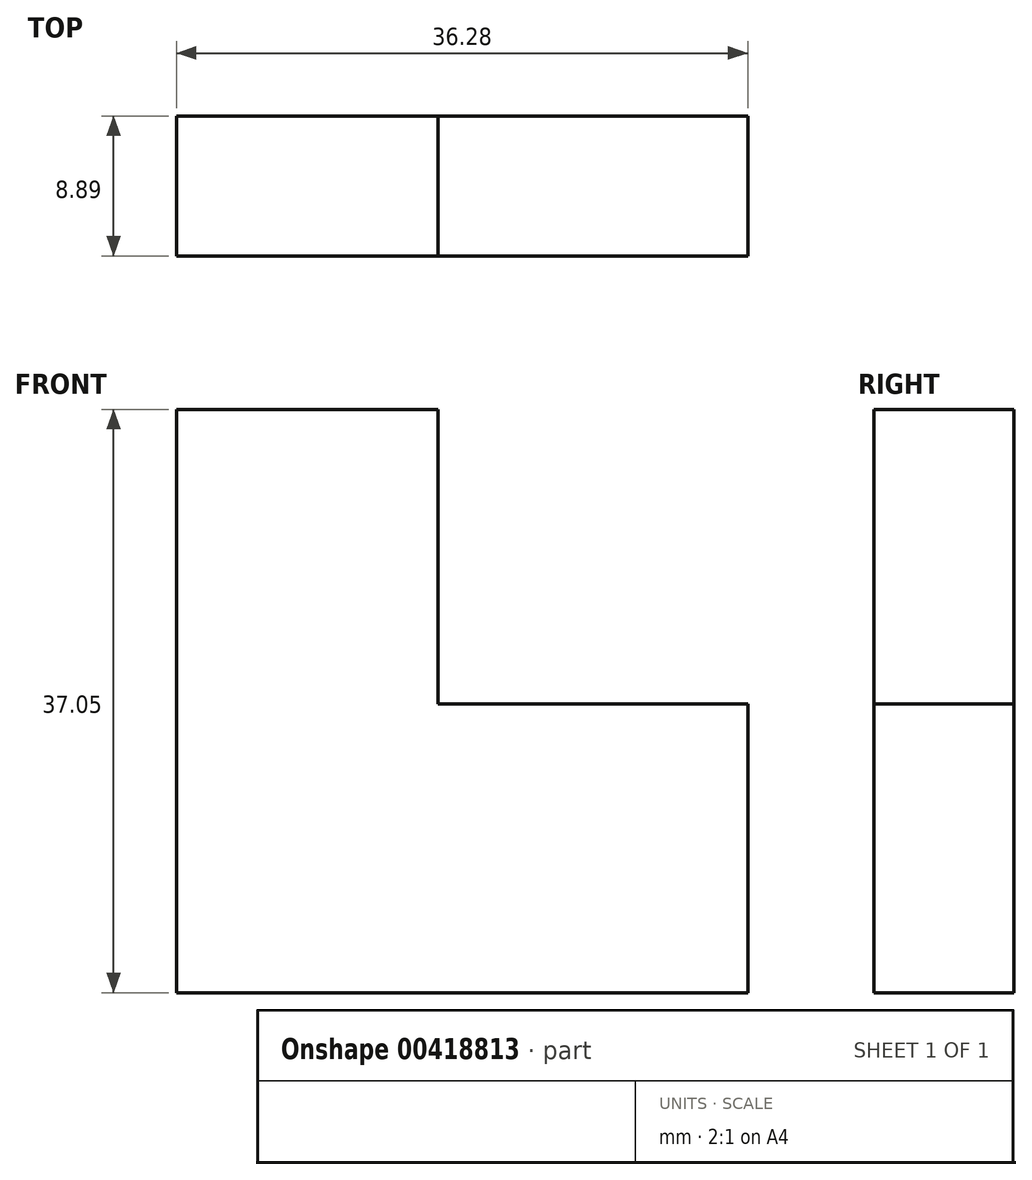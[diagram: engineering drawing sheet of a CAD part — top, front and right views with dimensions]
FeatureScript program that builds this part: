
annotation { "Feature Type Name" : "Feature", "Feature Type Description" : "" }
export const myFeature = defineFeature(function(context is Context, id is Id, definition is map)
    precondition{}
    {
        {
            var Q0;
            Q0=qCreatedBy(makeId("Front.planeOp"),FACE);
            var sketch = newSketch(context, id + "F0", { "sketchPlane" : qUnion([Q0])});
            skLineSegment(sketch, "E0", {"start": v(-36.28, 0) * mm, "end": v(-36.28, 37.05) * mm});
            skLineSegment(sketch, "E1", {"start": v(-36.28, 37.05) * mm, "end": v(-19.67, 37.05) * mm});
            skLineSegment(sketch, "E2", {"start": v(-19.67, 37.05) * mm, "end": v(-19.67, 18.33) * mm});
            skLineSegment(sketch, "E3", {"start": v(-19.67, 18.33) * mm, "end": v(0, 18.33) * mm});
            skLineSegment(sketch, "E4", {"start": v(0, 18.33) * mm, "end": v(0, 0) * mm});
            skLineSegment(sketch, "E5", {"start": v(0, 0) * mm, "end": v(-36.28, 0) * mm});
            skSolve(sketch);
        }
        {
            var Q0;
            Q0=makeQuery(id+"F0.imprint","IMPRINT",FACE,{"disambiguationData":[TD([[makeQuery(id+"F0.imprint","IMPRINT",EDGE,{"derivedFrom":sQuery(id+"F0.wireOp",EDGE,"E0")}),-1.0]])]});
            extrude(context, id + "F1", {"entities" : qUnion([Q0]), "depth" : 8.9 * mm});
        }
    });
